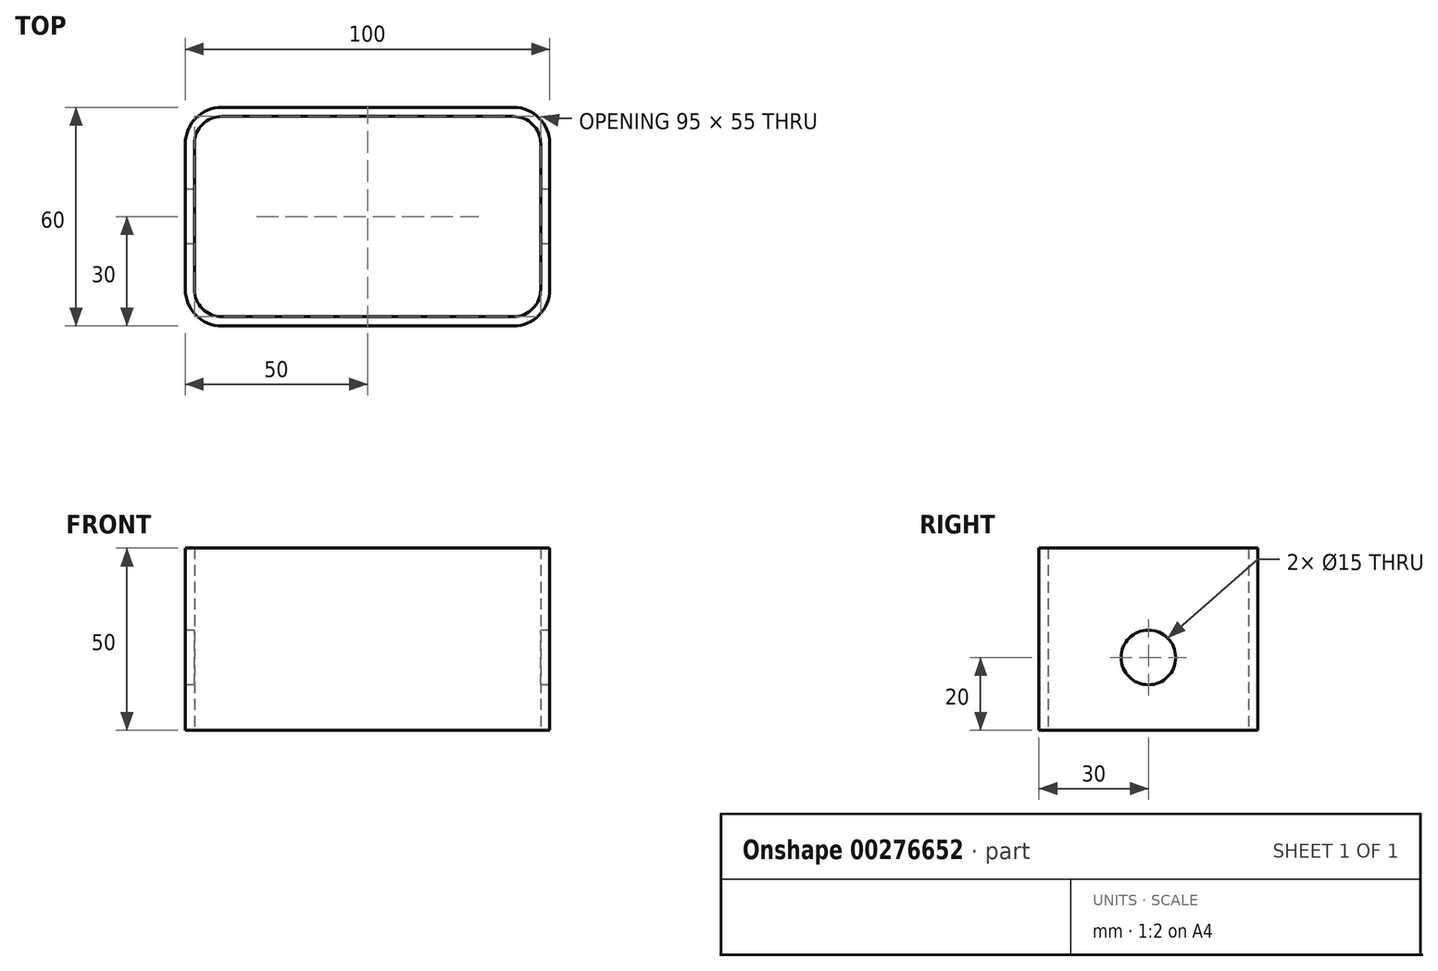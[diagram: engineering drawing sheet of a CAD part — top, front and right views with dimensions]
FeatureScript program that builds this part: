
annotation { "Feature Type Name" : "Feature", "Feature Type Description" : "" }
export const myFeature = defineFeature(function(context is Context, id is Id, definition is map)
    precondition{}
    {
        {
            var Q0;
            Q0=qCreatedBy(makeId("Top.planeOp"),FACE);
            var sketch = newSketch(context, id + "F0", { "sketchPlane" : qUnion([Q0])});
            skLineSegment(sketch, "E0.bottom", {"start": v(50, 30) * mm, "end": v(-50, 30) * mm});
            skLineSegment(sketch, "E0.top", {"start": v(50, -30) * mm, "end": v(-50, -30) * mm});
            skLineSegment(sketch, "E0.left", {"start": v(50, 30) * mm, "end": v(50, -30) * mm});
            skLineSegment(sketch, "E0.right", {"start": v(-50, 30) * mm, "end": v(-50, -30) * mm});
            skPoint(sketch, "E0.middle", {"position": v(0, 0) * mm});
            skSolve(sketch);
        }
        {
            var Q0;
            Q0 = qSketchRegion(id + "F0", true);
            extrude(context, id + "F1", {"entities" : qUnion([Q0]), "depth" : 50 * mm});
        }
        {
            var Q0;
            Q0=makeQuery(id+"F1.opExtrude","SWEPT_EDGE",EDGE,{"disambiguationData":[OSD([sQuery(id+"F0.wireOp",EDGE,"E0.top"),sQuery(id+"F0.wireOp",EDGE,"E0.left")])]});
            var Q1;
            Q1=makeQuery(id+"F1.opExtrude","SWEPT_EDGE",EDGE,{"disambiguationData":[OSD([sQuery(id+"F0.wireOp",EDGE,"E0.bottom"),sQuery(id+"F0.wireOp",EDGE,"E0.left")])]});
            var Q2;
            Q2=makeQuery(id+"F1.opExtrude","SWEPT_EDGE",EDGE,{"disambiguationData":[OSD([sQuery(id+"F0.wireOp",EDGE,"E0.bottom"),sQuery(id+"F0.wireOp",EDGE,"E0.right")])]});
            var Q3;
            Q3=makeQuery(id+"F1.opExtrude","SWEPT_EDGE",EDGE,{"disambiguationData":[OSD([sQuery(id+"F0.wireOp",EDGE,"E0.top"),sQuery(id+"F0.wireOp",EDGE,"E0.right")])]});
            fillet(context, id + "F2", {"entities" : qUnion([Q0, Q1, Q2, Q3]), "radius" : 10 * mm, "tangentPropagation" : true, "allowEdgeOverflow" : false});
        }
        {
            var Q0;
            Q0=makeQuery(id+"F1.opExtrude","CAP_FACE",FACE,{"disambiguationData":[OSD([sQuery(id+"F0.wireOp",EDGE,"E0.bottom"),sQuery(id+"F0.wireOp",EDGE,"E0.top"),sQuery(id+"F0.wireOp",EDGE,"E0.left"),sQuery(id+"F0.wireOp",EDGE,"E0.right")])],"isStart":false});
            var Q1;
            Q1=makeQuery(id+"F1.opExtrude","CAP_FACE",FACE,{"disambiguationData":[OSD([sQuery(id+"F0.wireOp",EDGE,"E0.bottom"),sQuery(id+"F0.wireOp",EDGE,"E0.top"),sQuery(id+"F0.wireOp",EDGE,"E0.left"),sQuery(id+"F0.wireOp",EDGE,"E0.right")])],"isStart":true});
            shell(context, id + "F3", {"entities" : qUnion([Q0, Q1]), "thickness" : 2.5 * mm});
        }
        {
            var Q0;
            Q0=makeQuery(id+"F1.opExtrude","SWEPT_FACE",FACE,{"disambiguationData":[OSD([sQuery(id+"F0.wireOp",EDGE,"E0.right")])]});
            var sketch = newSketch(context, id + "F4", { "sketchPlane" : qUnion([Q0])});
            skCircle(sketch, "E1", {"center": v(0, 20) * mm, "radius": 7.5 * mm});
            skSolve(sketch);
        }
        {
            var Q0;
            Q0=makeQuery(id+"F4.imprint","IMPRINT",FACE,{"disambiguationData":[TD([[makeQuery(id+"F4.imprint","IMPRINT",EDGE,{"derivedFrom":sQuery(id+"F4.wireOp",EDGE,"E1")}),1.0]])]});
            extrude(context, id + "F5", {"entities" : qUnion([Q0]), "operationType" : NewBodyOperationType.REMOVE, "oppositeDirection" : true, "depth" : 119.1 * mm});
        }
    });
